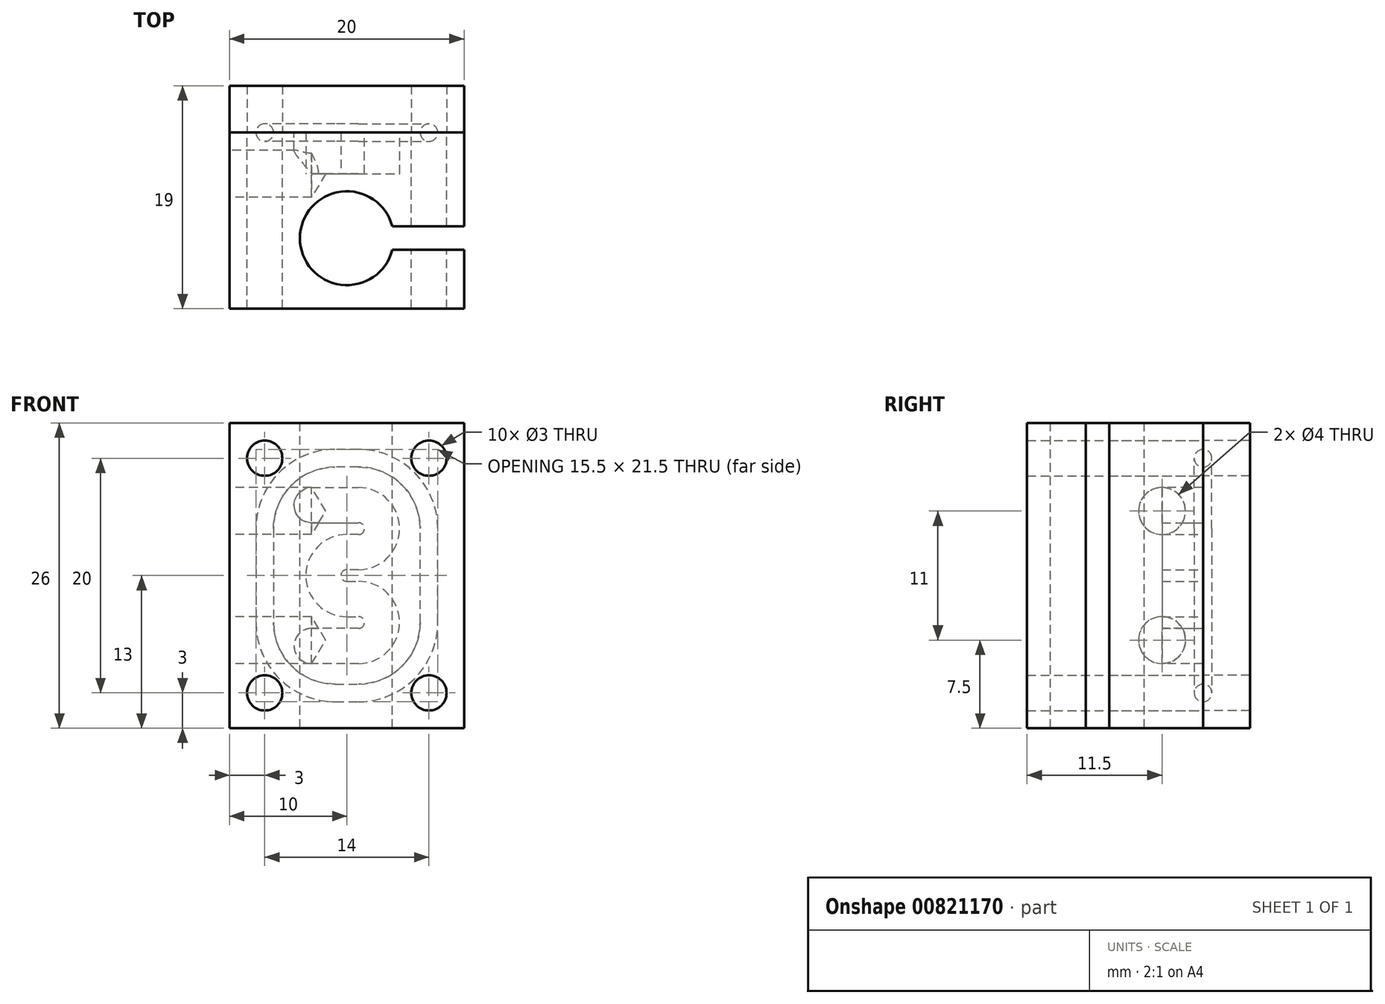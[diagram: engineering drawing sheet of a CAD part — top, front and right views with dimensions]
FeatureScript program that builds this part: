
annotation { "Feature Type Name" : "Feature", "Feature Type Description" : "" }
export const myFeature = defineFeature(function(context is Context, id is Id, definition is map)
    precondition{}
    {
        {
            var Q0;
            Q0=qCreatedBy(makeId("Top.planeOp"),FACE);
            var sketch = newSketch(context, id + "F0", { "sketchPlane" : qUnion([Q0])});
            skLineSegment(sketch, "E0.bottom", {"start": v(-26.95, 5.5) * mm, "end": v(-6.95, 5.5) * mm});
            skLineSegment(sketch, "E0.top", {"start": v(-26.95, 20.5) * mm, "end": v(-6.95, 20.5) * mm});
            skLineSegment(sketch, "E0.left", {"start": v(-26.95, 5.5) * mm, "end": v(-26.95, 20.5) * mm});
            skLineSegment(sketch, "E0.right", {"start": v(-6.95, 5.5) * mm, "end": v(-6.95, 20.5) * mm});
            skCircle(sketch, "E1.0", {"center": v(-16.95, 11.5) * mm, "radius": 4 * mm});
            skLineSegment(sketch, "E2", {"start": v(-13.08, 10.5) * mm, "end": v(-6.95, 10.5) * mm});
            skLineSegment(sketch, "E3", {"start": v(-13.08, 12.5) * mm, "end": v(-6.95, 12.5) * mm});
            skSolve(sketch);
        }
        {
            var Q0;
            {var subQ1=sQuery(id+"F0.wireOp",EDGE,"E0.bottom");Q0=makeQuery(id+"F0.imprint","IMPRINT",FACE,{"disambiguationData":[TD([[makeQuery(id+"F0.imprint","IMPRINT",EDGE,{"derivedFrom":subQ1}),1.0]])]});}
            extrude(context, id + "F1", {"entities" : qUnion([Q0]), "oppositeDirection" : true, "depth" : 26 * mm, "offsetDistance" : 25 * mm});
        }
        {
            var Q0;
            Q0=makeQuery(id+"F1.opExtrude","SWEPT_FACE",FACE,{"disambiguationData":[OSD([sQuery(id+"F0.wireOp",EDGE,"E0.top")])]});
            var sketch = newSketch(context, id + "F2", { "sketchPlane" : qUnion([Q0])});
            skPoint(sketch, "E4", {"position": v(9.95, -23) * mm});
            skPoint(sketch, "E5.0.1.0", {"position": v(9.95, -13) * mm});
            skPoint(sketch, "E5.0.2.0", {"position": v(9.95, -3) * mm});
            skPoint(sketch, "E5.1.0.0", {"position": v(23.95, -23) * mm});
            skPoint(sketch, "E5.1.1.0", {"position": v(23.95, -13) * mm});
            skPoint(sketch, "E5.1.2.0", {"position": v(23.95, -3) * mm});
            skLineSegment(sketch, "E5.direction1", {"start": v(9.95, -23) * mm, "end": v(23.95, -23) * mm, "construction": true});
            skLineSegment(sketch, "E5.direction2", {"start": v(9.95, -23) * mm, "end": v(9.95, -13) * mm, "construction": true});
            skSolve(sketch);
        }
        {
            var Q0;
            Q0=sQuery(id+"F2.wireOp",VERTEX,"E4");
            var Q1;
            Q1=sQuery(id+"F2.wireOp",VERTEX,"E5.0.2.0");
            var Q2;
            Q2=sQuery(id+"F2.wireOp",VERTEX,"E5.1.0.0");
            var Q3;
            Q3=sQuery(id+"F2.wireOp",VERTEX,"E5.1.2.0");
            var Q4;
            Q4=makeQuery(id+"F1.opExtrude","SWEPT_BODY",BODY,{"disambiguationData":[OSD([sQuery(id+"F0.wireOp",EDGE,"E0.bottom"),sQuery(id+"F0.wireOp",EDGE,"E0.top"),sQuery(id+"F0.wireOp",EDGE,"E0.left"),sQuery(id+"F0.wireOp",EDGE,"E0.right"),sQuery(id+"F0.wireOp",EDGE,"E1.0"),sQuery(id+"F0.wireOp",EDGE,"E2"),sQuery(id+"F0.wireOp",EDGE,"E3")])]});
            hole(context, id + "F3", {"style" : HoleStyle.SIMPLE, "endStyle" : HoleEndStyle.THROUGH, "standardTappedOrClearance" : lookupTablePath({ "standard" : "ISO", "size" : "3", "type" : "Drilled" }), "standardBlindInLast" : lookupTablePath({ "standard" : "ISO", "size" : "3", "type" : "Drilled" }), "holeDiameter" : 3 * mm, "majorDiameter" : 5 * mm, "isTappedThrough" : true, "tappedDepth" : 6 * mm, "tapClearance" : 3, "startFromSketch" : true, "locations" : qUnion([Q0, Q1, Q2, Q3]), "scope" : qUnion([Q4])});
        }
        {
            var Q0;
            Q0=makeQuery(id+"F1.opExtrude","SWEPT_FACE",FACE,{"disambiguationData":[OSD([sQuery(id+"F0.wireOp",EDGE,"E0.top")])]});
            var sketch = newSketch(context, id + "F4", { "sketchPlane" : qUnion([Q0])});
            skLineSegment(sketch, "E6", {"start": v(21.45, -19) * mm, "end": v(15.95, -19) * mm});
            skLineSegment(sketch, "E7", {"start": v(13.95, -17) * mm, "end": v(13.95, -17) * mm});
            skLineSegment(sketch, "E8", {"start": v(18.95, -13) * mm, "end": v(18.95, -13) * mm});
            skLineSegment(sketch, "E9", {"start": v(16.95, -11) * mm, "end": v(15.95, -11) * mm});
            skLineSegment(sketch, "E10", {"start": v(13.95, -9) * mm, "end": v(13.95, -9) * mm});
            skLineSegment(sketch, "E11", {"start": v(15.95, -7) * mm, "end": v(21.45, -7) * mm});
            skLineSegment(sketch, "E12", {"start": v(16.95, -15) * mm, "end": v(15.95, -15) * mm});
            skPoint(sketch, "E13.visualSharp", {"position": v(13.95, -19) * mm});
            skArc(sketch, "E13.filletArc", {"start": v(13.95, -17) * mm, "mid": v(14.54, -18.41) * mm, "end": v(15.95, -19) * mm});
            skPoint(sketch, "E14.visualSharp", {"position": v(13.95, -15) * mm});
            skArc(sketch, "E14.filletArc", {"start": v(15.95, -15) * mm, "mid": v(14.54, -15.59) * mm, "end": v(13.95, -17) * mm});
            skPoint(sketch, "E15.visualSharp", {"position": v(18.95, -15) * mm});
            skArc(sketch, "E15.filletArc", {"start": v(16.95, -15) * mm, "mid": v(18.36, -14.41) * mm, "end": v(18.95, -13) * mm});
            skPoint(sketch, "E16.visualSharp", {"position": v(18.95, -11) * mm});
            skArc(sketch, "E16.filletArc", {"start": v(18.95, -13) * mm, "mid": v(18.36, -11.59) * mm, "end": v(16.95, -11) * mm});
            skPoint(sketch, "E17.visualSharp", {"position": v(13.95, -11) * mm});
            skArc(sketch, "E17.filletArc", {"start": v(13.95, -9) * mm, "mid": v(14.54, -10.41) * mm, "end": v(15.95, -11) * mm});
            skPoint(sketch, "E18.visualSharp", {"position": v(13.95, -7) * mm});
            skArc(sketch, "E18.filletArc", {"start": v(15.95, -7) * mm, "mid": v(14.54, -7.59) * mm, "end": v(13.95, -9) * mm});
            skPoint(sketch, "E19", {"position": v(19.45, -19) * mm});
            skPoint(sketch, "E20", {"position": v(19.45, -7) * mm});
            skSolve(sketch);
        }
        {
            var Q0;
            Q0=qCreatedBy(makeId("Right.planeOp"),FACE);
            cPlane(context, id + "F5", {"entities" : qUnion([Q0]), "cplaneType" : CPlaneType.OFFSET, "offset" : 16.95 * mm, "oppositeDirection" : true, "width" : 150 * mm, "height" : 150 * mm});
        }
        {
            var Q0;
            Q0=qCreatedBy(id+"F5.planeOp",FACE);
            var sketch = newSketch(context, id + "F6", { "sketchPlane" : qUnion([Q0])});
            skPoint(sketch, "E21.0", {"position": v(20.5, -7) * mm});
            skLineSegment(sketch, "E22.bottom", {"start": v(17, -8.5) * mm, "end": v(24, -8.5) * mm});
            skLineSegment(sketch, "E22.top", {"start": v(17, -5.5) * mm, "end": v(24, -5.5) * mm});
            skLineSegment(sketch, "E22.left", {"start": v(17, -8.5) * mm, "end": v(17, -5.5) * mm});
            skLineSegment(sketch, "E22.right", {"start": v(24, -8.5) * mm, "end": v(24, -5.5) * mm});
            skSolve(sketch);
        }
        {
            var Q0;
            Q0=makeQuery(id+"F6.imprint","IMPRINT",FACE,{"disambiguationData":[TD([[makeQuery(id+"F6.imprint","IMPRINT",EDGE,{"derivedFrom":sQuery(id+"F6.wireOp",EDGE,"E22.bottom")}),1.0]])]});
            var Q1;
            Q1=sQuery(id+"F4.wireOp",EDGE,"E11");
            var Q2;
            Q2=sQuery(id+"F4.wireOp",EDGE,"E18.filletArc");
            var Q3;
            Q3=sQuery(id+"F4.wireOp",EDGE,"E10");
            var Q4;
            Q4=sQuery(id+"F4.wireOp",EDGE,"E17.filletArc");
            var Q5;
            Q5=sQuery(id+"F4.wireOp",EDGE,"E9");
            var Q6;
            Q6=sQuery(id+"F4.wireOp",EDGE,"E16.filletArc");
            var Q7;
            Q7=sQuery(id+"F4.wireOp",EDGE,"E8");
            var Q8;
            Q8=sQuery(id+"F4.wireOp",EDGE,"E15.filletArc");
            var Q9;
            Q9=sQuery(id+"F4.wireOp",EDGE,"E12");
            var Q10;
            Q10=sQuery(id+"F4.wireOp",EDGE,"E14.filletArc");
            var Q11;
            Q11=sQuery(id+"F4.wireOp",EDGE,"E7");
            var Q12;
            Q12=sQuery(id+"F4.wireOp",EDGE,"E13.filletArc");
            var Q13;
            Q13=sQuery(id+"F4.wireOp",EDGE,"E6");
            sweep(context, id + "F7", {"operationType" : NewBodyOperationType.REMOVE, "profiles" : qUnion([Q0]), "path" : qUnion([Q1, Q2, Q3, Q4, Q5, Q6, Q7, Q8, Q9, Q10, Q11, Q12, Q13])});
        }
        {
            var Q0;
            Q0=makeQuery(id+"F7.boolean.opBoolean","COPY",EDGE,{"derivedFrom":makeQuery(id+"F7.opSweep","CAP_EDGE",EDGE,{"disambiguationData":[OSD([sQuery(id+"F4.wireOp",VERTEX,"E11.end"),sQuery(id+"F6.wireOp",EDGE,"E22.top")])],"isStart":true})});
            var Q1;
            Q1=makeQuery(id+"F7.boolean.opBoolean","COPY",EDGE,{"derivedFrom":makeQuery(id+"F7.opSweep","CAP_EDGE",EDGE,{"disambiguationData":[OSD([sQuery(id+"F4.wireOp",VERTEX,"E11.end"),sQuery(id+"F6.wireOp",EDGE,"E22.bottom")])],"isStart":true})});
            var Q2;
            Q2=makeQuery(id+"F7.boolean.opBoolean","COPY",EDGE,{"derivedFrom":makeQuery(id+"F7.opSweep","CAP_EDGE",EDGE,{"disambiguationData":[OSD([sQuery(id+"F4.wireOp",VERTEX,"E6.start"),sQuery(id+"F6.wireOp",EDGE,"E22.top")])],"isStart":false})});
            var Q3;
            Q3=makeQuery(id+"F7.boolean.opBoolean","COPY",EDGE,{"derivedFrom":makeQuery(id+"F7.opSweep","CAP_EDGE",EDGE,{"disambiguationData":[OSD([sQuery(id+"F4.wireOp",VERTEX,"E6.start"),sQuery(id+"F6.wireOp",EDGE,"E22.bottom")])],"isStart":false})});
            fillet(context, id + "F8", {"entities" : qUnion([Q0, Q1, Q2, Q3]), "radius" : 1.5 * mm, "tangentPropagation" : true, "allowEdgeOverflow" : false});
        }
        {
            var Q0;
            Q0=makeQuery(id+"F1.opExtrude","SWEPT_FACE",FACE,{"disambiguationData":[OSD([sQuery(id+"F0.wireOp",EDGE,"E0.left")])]});
            var sketch = newSketch(context, id + "F9", { "sketchPlane" : qUnion([Q0])});
            skPoint(sketch, "E23", {"position": v(-17, -18.5) * mm});
            skPoint(sketch, "E24", {"position": v(-17, -7.5) * mm});
            skSolve(sketch);
        }
        {
            var Q0;
            Q0=sQuery(id+"F9.wireOp",VERTEX,"E24");
            var Q1;
            Q1=sQuery(id+"F9.wireOp",VERTEX,"E23");
            var Q2;
            Q2=makeQuery(id+"F1.opExtrude","SWEPT_BODY",BODY,{"disambiguationData":[OSD([sQuery(id+"F0.wireOp",EDGE,"E0.bottom"),sQuery(id+"F0.wireOp",EDGE,"E0.top"),sQuery(id+"F0.wireOp",EDGE,"E0.left"),sQuery(id+"F0.wireOp",EDGE,"E0.right"),sQuery(id+"F0.wireOp",EDGE,"E1.0"),sQuery(id+"F0.wireOp",EDGE,"E2"),sQuery(id+"F0.wireOp",EDGE,"E3")])]});
            hole(context, id + "F10", {"style" : HoleStyle.SIMPLE, "endStyle" : HoleEndStyle.BLIND, "holeDiameter" : 4 * mm, "majorDiameter" : 5 * mm, "holeDepth" : 7 * mm, "isTappedThrough" : true, "tappedDepth" : 6 * mm, "tapClearance" : 3, "startFromSketch" : true, "locations" : qUnion([Q0, Q1]), "scope" : qUnion([Q2])});
        }
        {
            var Q0;
            Q0=makeQuery(id+"F1.opExtrude","SWEPT_FACE",FACE,{"disambiguationData":[OSD([sQuery(id+"F0.wireOp",EDGE,"E0.bottom")])]});
            var Q1;
            Q1=makeQuery(id+"F1.opExtrude","SWEPT_FACE",FACE,{"disambiguationData":[OSD([sQuery(id+"F0.wireOp",EDGE,"E0.top")])]});
            var Q2;
            Q2=makeQuery(id+"F1.opExtrude","SWEPT_FACE",FACE,{"disambiguationData":[OSD([sQuery(id+"F0.wireOp",EDGE,"E0.top")])]});
            extrude(context, id + "F11", {"entities" : qUnion([Q0]), "endBound" : BoundingType.UP_TO_SURFACE, "oppositeDirection" : true, "depth" : 25 * mm, "endBoundEntityFace" : qUnion([Q1]), "hasOffset" : true, "offsetDistance" : 4 * mm, "offsetOppositeDirection" : true, "hasSecondDirection" : true, "secondDirectionBound" : SecondDirectionBoundingType.UP_TO_SURFACE, "secondDirectionOppositeDirection" : true, "secondDirectionDepth" : 25 * mm, "secondDirectionBoundEntityFace" : qUnion([Q2])});
        }
        {
            var Q0;
            Q0=makeQuery(id+"F1.opExtrude","SWEPT_FACE",FACE,{"disambiguationData":[OSD([sQuery(id+"F0.wireOp",EDGE,"E0.top")])]});
            var sketch = newSketch(context, id + "F12", { "sketchPlane" : qUnion([Q0])});
            skLineSegment(sketch, "E25.bottom", {"start": v(17.95, -23) * mm, "end": v(15.95, -23) * mm});
            skLineSegment(sketch, "E25.top", {"start": v(17.95, -3) * mm, "end": v(15.95, -3) * mm});
            skLineSegment(sketch, "E25.left", {"start": v(23.95, -17) * mm, "end": v(23.95, -9) * mm});
            skLineSegment(sketch, "E25.right", {"start": v(9.95, -17) * mm, "end": v(9.95, -9) * mm});
            skPoint(sketch, "E26.visualSharp", {"position": v(9.95, -23) * mm});
            skArc(sketch, "E26.filletArc", {"start": v(9.95, -17) * mm, "mid": v(11.7, -21.24) * mm, "end": v(15.95, -23) * mm});
            skPoint(sketch, "E27.visualSharp", {"position": v(23.95, -23) * mm});
            skArc(sketch, "E27.filletArc", {"start": v(17.95, -23) * mm, "mid": v(22.2, -21.24) * mm, "end": v(23.95, -17) * mm});
            skPoint(sketch, "E28.visualSharp", {"position": v(23.95, -3) * mm});
            skArc(sketch, "E28.filletArc", {"start": v(23.95, -9) * mm, "mid": v(22.2, -4.76) * mm, "end": v(17.95, -3) * mm});
            skPoint(sketch, "E29.visualSharp", {"position": v(9.95, -3) * mm});
            skArc(sketch, "E29.filletArc", {"start": v(15.95, -3) * mm, "mid": v(11.7, -4.76) * mm, "end": v(9.95, -9) * mm});
            skSolve(sketch);
        }
        {
            var Q0;
            Q0=qCreatedBy(id+"F5.planeOp",FACE);
            var sketch = newSketch(context, id + "F13", { "sketchPlane" : qUnion([Q0])});
            skPoint(sketch, "E30.0", {"position": v(20.5, -23) * mm});
            skCircle(sketch, "E31", {"center": v(20.5, -23) * mm, "radius": 0.75 * mm});
            skSolve(sketch);
        }
        {
            var Q0;
            Q0=makeQuery(id+"F13.imprint","IMPRINT",FACE,{"disambiguationData":[TD([[makeQuery(id+"F13.imprint","IMPRINT",EDGE,{"derivedFrom":sQuery(id+"F13.wireOp",EDGE,"E31")}),1.0]])]});
            var Q1;
            Q1=qConstructionFilter(qBodyType(qCreatedBy(id+"F12",EDGE),BodyType.WIRE),ConstructionObject.NO);
            sweep(context, id + "F14", {"operationType" : NewBodyOperationType.REMOVE, "profiles" : qUnion([Q0]), "path" : qUnion([Q1])});
        }
        {
            var Q0;
            Q0=makeQuery(id+"F13.imprint","IMPRINT",FACE,{"disambiguationData":[TD([[makeQuery(id+"F13.imprint","IMPRINT",EDGE,{"derivedFrom":sQuery(id+"F13.wireOp",EDGE,"E31")}),1.0]])]});
            var Q1;
            Q1=sQuery(id+"F13.wireOp",EDGE,"E31");
            var Q2;
            Q2=qConstructionFilter(qBodyType(qCreatedBy(id+"F12",EDGE),BodyType.WIRE),ConstructionObject.NO);
            sweep(context, id + "F15", {"profiles" : qUnion([Q0]), "surfaceProfiles" : qUnion([Q1]), "path" : qUnion([Q2])});
        }
    });
